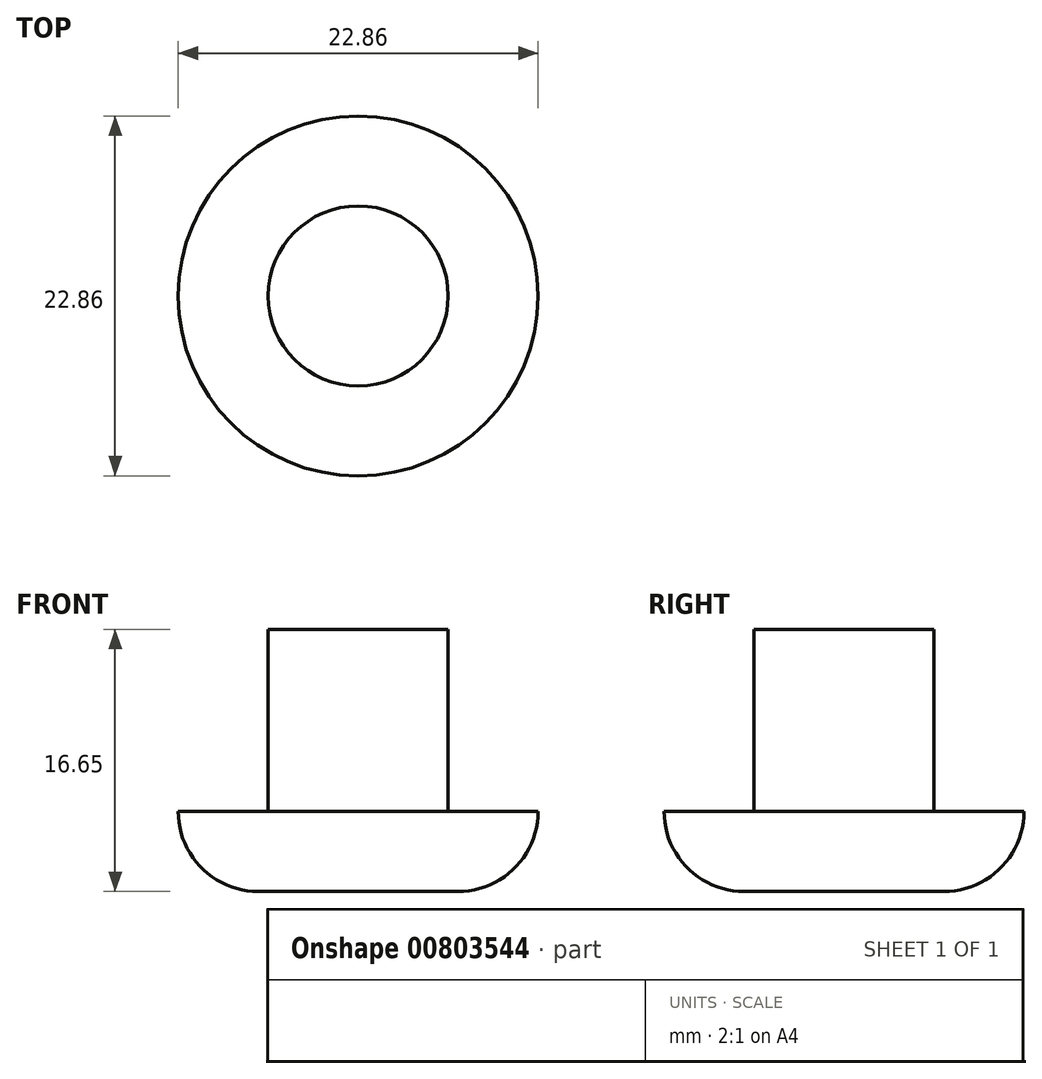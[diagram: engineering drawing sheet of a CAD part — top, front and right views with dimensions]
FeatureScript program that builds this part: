
annotation { "Feature Type Name" : "Feature", "Feature Type Description" : "" }
export const myFeature = defineFeature(function(context is Context, id is Id, definition is map)
    precondition{}
    {
        {
            var Q0;
            Q0=qCreatedBy(makeId("Top.planeOp"),FACE);
            var sketch = newSketch(context, id + "F0", { "sketchPlane" : qUnion([Q0])});
            skCircle(sketch, "E0", {"center": v(0, 0) * mm, "radius": 11.43 * mm});
            skSolve(sketch);
        }
        {
            var Q0;
            Q0=makeQuery(id+"F0.imprint","IMPRINT",FACE,{"disambiguationData":[TD([[makeQuery(id+"F0.imprint","IMPRINT",EDGE,{"derivedFrom":sQuery(id+"F0.wireOp",EDGE,"E0")}),1.0]])]});
            extrude(context, id + "F1", {"entities" : qUnion([Q0]), "depth" : 5.08 * mm, "offsetDistance" : 25.4 * mm});
        }
        {
            var Q0;
            Q0=makeQuery(id+"F1.opExtrude","CAP_EDGE",EDGE,{"disambiguationData":[OSD([sQuery(id+"F0.wireOp",EDGE,"E0")])],"isStart":true});
            fillet(context, id + "F2", {"entities" : qUnion([Q0]), "radius" : 5.08 * mm, "tangentPropagation" : true, "allowEdgeOverflow" : false});
        }
        {
            var Q0;
            Q0=makeQuery(id+"F1.opExtrude","CAP_FACE",FACE,{"disambiguationData":[OSD([sQuery(id+"F0.wireOp",EDGE,"E0")])],"isStart":false});
            var sketch = newSketch(context, id + "F3", { "sketchPlane" : qUnion([Q0])});
            skCircle(sketch, "E1", {"center": v(0, 0) * mm, "radius": 5.72 * mm});
            skSolve(sketch);
        }
        {
            var Q0;
            Q0=makeQuery(id+"F3.imprint","IMPRINT",FACE,{"disambiguationData":[TD([[makeQuery(id+"F3.imprint","IMPRINT",EDGE,{"derivedFrom":sQuery(id+"F3.wireOp",EDGE,"E1")}),1.0]])]});
            extrude(context, id + "F4", {"entities" : qUnion([Q0]), "operationType" : NewBodyOperationType.ADD, "depth" : 11.57 * mm, "offsetDistance" : 25.4 * mm});
        }
    });
